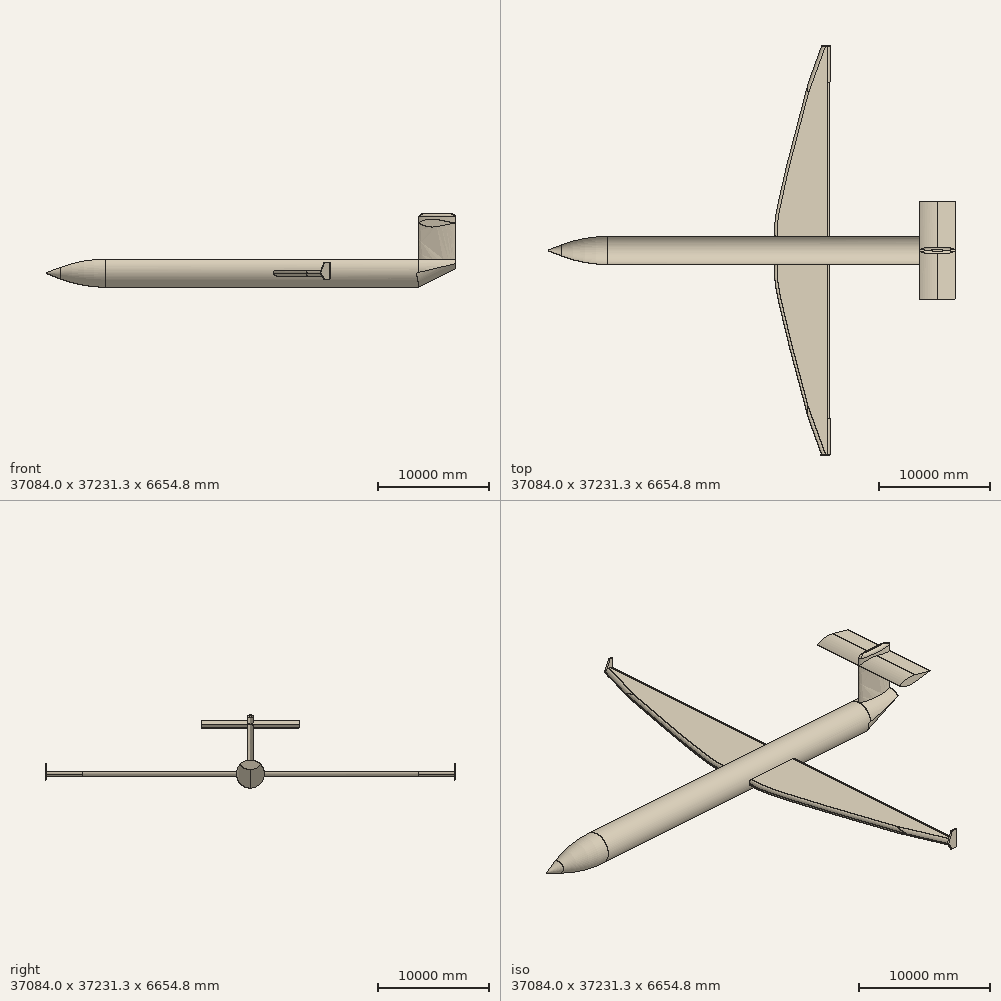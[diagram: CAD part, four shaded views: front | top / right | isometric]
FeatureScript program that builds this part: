
annotation { "Feature Type Name" : "Feature", "Feature Type Description" : "" }
export const myFeature = defineFeature(function(context is Context, id is Id, definition is map)
    precondition{}
    {
        {
            var Q0;
            Q0=qCreatedBy(makeId("Right.planeOp"),FACE);
            var sketch = newSketch(context, id + "F0", { "sketchPlane" : qUnion([Q0])});
            skCircle(sketch, "E0", {"center": v(0, 0) * mm, "radius": 1270 * mm});
            skSolve(sketch);
        }
        {
            var Q0;
            Q0=makeQuery(id+"F0.imprint","IMPRINT",FACE,{"disambiguationData":[TD([[makeQuery(id+"F0.imprint","IMPRINT",EDGE,{"derivedFrom":sQuery(id+"F0.wireOp",EDGE,"E0")}),1.0]])]});
            extrude(context, id + "F1", {"entities" : qUnion([Q0]), "endBound" : BoundingType.SYMMETRIC, "oppositeDirection" : true, "depth" : 30480 * mm, "offsetDistance" : 25.4 * mm});
        }
        {
            var Q0;
            Q0=qCreatedBy(makeId("Front.planeOp"),FACE);
            var sketch = newSketch(context, id + "F2", { "sketchPlane" : qUnion([Q0])});
            skLineSegment(sketch, "E1", {"start": v(0, 0) * mm, "end": v(0, 1270) * mm});
            skLineSegment(sketch, "E2", {"start": v(0, 1270) * mm, "end": v(15240, 1270) * mm});
            skLineSegment(sketch, "E3", {"start": v(15240, 1270) * mm, "end": v(15240, -1270) * mm});
            skLineSegment(sketch, "E4", {"start": v(15240, 1270) * mm, "end": v(18542, 1270) * mm});
            skLineSegment(sketch, "E5", {"start": v(15240, -1270) * mm, "end": v(18542, 400.65) * mm});
            skLineSegment(sketch, "E6", {"start": v(18542, 400.65) * mm, "end": v(18542, 1270) * mm});
            skSolve(sketch);
        }
        {
            var Q0;
            Q0 = qSketchRegion(id + "F2", true);
            extrude(context, id + "F3", {"entities" : qUnion([Q0]), "operationType" : NewBodyOperationType.ADD, "endBound" : BoundingType.SYMMETRIC, "depth" : 2540 * mm, "offsetDistance" : 25.4 * mm});
        }
        {
            var Q0;
            Q0=makeQuery(id+"F3.opExtrude","CAP_EDGE",EDGE,{"disambiguationData":[OSD([sQuery(id+"F2.wireOp",EDGE,"E4")])],"isStart":false});
            var Q1;
            Q1=makeQuery(id+"F3.opExtrude","CAP_EDGE",EDGE,{"disambiguationData":[OSD([sQuery(id+"F2.wireOp",EDGE,"E4")])],"isStart":true});
            var Q2;
            Q2=makeQuery(id+"F3.opExtrude","CAP_EDGE",EDGE,{"disambiguationData":[OSD([sQuery(id+"F2.wireOp",EDGE,"E5")])],"isStart":false});
            var Q3;
            Q3=makeQuery(id+"F3.opExtrude","CAP_EDGE",EDGE,{"disambiguationData":[OSD([sQuery(id+"F2.wireOp",EDGE,"E5")])],"isStart":true});
            fillet(context, id + "F4", {"entities" : qUnion([Q0, Q1, Q2, Q3]), "radius" : 1244.6 * mm, "tangentPropagation" : true, "allowEdgeOverflow" : false});
        }
        {
            var Q0;
            Q0=makeQuery(id+"F3.opExtrude","SWEPT_FACE",FACE,{"disambiguationData":[OSD([sQuery(id+"F2.wireOp",EDGE,"E4")])]});
            var sketch = newSketch(context, id + "F5", { "sketchPlane" : qUnion([Q0])});
            skEllipse(sketch, "E7", {"center": v(16891, 0) * mm, "majorRadius": 1651 * mm, "minorRadius": 317.5 * mm, "majorAxis": v(-1, 0)});
            skPoint(sketch, "E7.centerSnap0", {"position": v(16891, 25.4) * mm});
            skSolve(sketch);
        }
        {
            var Q0;
            Q0=qCreatedBy(makeId("Top.planeOp"),FACE);
            var sketch = newSketch(context, id + "F6", { "sketchPlane" : qUnion([Q0])});
            skLineSegment(sketch, "E8", {"start": v(5164.79, 15221.95) * mm, "end": v(7114.72, 15221.95) * mm});
            skLineSegment(sketch, "E9", {"start": v(7114.72, -15229.4) * mm, "end": v(5164.79, -15229.4) * mm});
            skFitSpline(sketch, "E10", {"points": [v(2139.22, 1285.92) * mm, v(2139.22, 2711.9) * mm, v(5164.79, 15221.95) * mm], "startDerivative": vector(-498.9, 4287.93) * mm, "endDerivative": vector(5531.34, 20770.7) * mm});
            skFitSpline(sketch, "E11", {"points": [v(2131.34, -1268.74) * mm, v(2131.34, -2790.45) * mm, v(5164.79, -15229.4) * mm], "startDerivative": vector(-524.47, -4573.38) * mm, "endDerivative": vector(5598.9, -20746.14) * mm});
            skLineSegment(sketch, "E12", {"start": v(7114.72, -1259.38) * mm, "end": v(7114.72, -15229.4) * mm});
            skLineSegment(sketch, "E13", {"start": v(7114.72, 1309.17) * mm, "end": v(7114.72, 15221.95) * mm});
            skLineSegment(sketch, "E14", {"start": v(7114.72, 1309.17) * mm, "end": v(7114.72, -1259.38) * mm});
            skLineSegment(sketch, "E15", {"start": v(2139.22, 1285.92) * mm, "end": v(2131.34, -1268.74) * mm});
            skSolve(sketch);
        }
        {
            var Q0;
            Q0 = qSketchRegion(id + "F6", true);
            extrude(context, id + "F7", {"entities" : qUnion([Q0]), "operationType" : NewBodyOperationType.ADD, "endBound" : BoundingType.SYMMETRIC, "depth" : 508 * mm, "offsetDistance" : 25.4 * mm});
        }
        {
            var Q0;
            {var subQ0=sQuery(id+"F6.wireOp",EDGE,"E15");var subQ1=sQuery(id+"F6.wireOp",EDGE,"E10");Q0=makeQuery(id+"F7.boolean.opBoolean","SPLIT",EDGE,{"disambiguationData":[TD([makeQuery(id+"F7.opExtrude","SWEPT_FACE",FACE,{"disambiguationData":[OSD([subQ1])]})])],"derivedFrom":makeQuery(id+"F7.opExtrude","CAP_EDGE",EDGE,{"disambiguationData":[OSD([subQ0])],"isStart":true})});}
            var Q1;
            Q1=makeQuery(id+"F7.opExtrude","CAP_EDGE",EDGE,{"disambiguationData":[OSD([sQuery(id+"F6.wireOp",EDGE,"E10")])],"isStart":true});
            var Q2;
            {var subQ0=sQuery(id+"F6.wireOp",EDGE,"E15");var subQ1=sQuery(id+"F6.wireOp",EDGE,"E10");Q2=makeQuery(id+"F7.boolean.opBoolean","SPLIT",EDGE,{"disambiguationData":[TD([makeQuery(id+"F7.opExtrude","SWEPT_FACE",FACE,{"disambiguationData":[OSD([subQ1])]})])],"derivedFrom":makeQuery(id+"F7.opExtrude","CAP_EDGE",EDGE,{"disambiguationData":[OSD([subQ0])],"isStart":false})});}
            var Q3;
            Q3=makeQuery(id+"F7.opExtrude","CAP_EDGE",EDGE,{"disambiguationData":[OSD([sQuery(id+"F6.wireOp",EDGE,"E10")])],"isStart":false});
            fillet(context, id + "F8", {"entities" : qUnion([Q0, Q1, Q2, Q3]), "radius" : 254 * mm, "tangentPropagation" : true, "allowEdgeOverflow" : false});
        }
        {
            var Q0;
            Q0=makeQuery(id+"F7.opExtrude","CAP_EDGE",EDGE,{"disambiguationData":[OSD([sQuery(id+"F6.wireOp",EDGE,"E11")])],"isStart":false});
            var Q1;
            Q1=makeQuery(id+"F7.opExtrude","CAP_EDGE",EDGE,{"disambiguationData":[OSD([sQuery(id+"F6.wireOp",EDGE,"E11")])],"isStart":true});
            var Q2;
            {var subQ0=sQuery(id+"F6.wireOp",EDGE,"E15");var subQ1=sQuery(id+"F6.wireOp",EDGE,"E11");Q2=makeQuery(id+"F7.boolean.opBoolean","SPLIT",EDGE,{"disambiguationData":[TD([makeQuery(id+"F7.opExtrude","SWEPT_FACE",FACE,{"disambiguationData":[OSD([subQ1])]})])],"derivedFrom":makeQuery(id+"F7.opExtrude","CAP_EDGE",EDGE,{"disambiguationData":[OSD([subQ0])],"isStart":true})});}
            var Q3;
            {var subQ0=sQuery(id+"F6.wireOp",EDGE,"E15");var subQ1=sQuery(id+"F6.wireOp",EDGE,"E11");Q3=makeQuery(id+"F7.boolean.opBoolean","SPLIT",EDGE,{"disambiguationData":[TD([makeQuery(id+"F7.opExtrude","SWEPT_FACE",FACE,{"disambiguationData":[OSD([subQ1])]})])],"derivedFrom":makeQuery(id+"F7.opExtrude","CAP_EDGE",EDGE,{"disambiguationData":[OSD([subQ0])],"isStart":false})});}
            fillet(context, id + "F9", {"entities" : qUnion([Q0, Q1, Q2, Q3]), "radius" : 254 * mm, "tangentPropagation" : true, "allowEdgeOverflow" : false});
        }
        {
            var Q0;
            {var subQ0=sQuery(id+"F6.wireOp",EDGE,"E9");var subQ1=sQuery(id+"F6.wireOp",EDGE,"E14");var subQ2=sQuery(id+"F6.wireOp",EDGE,"E13");var subQ3=sQuery(id+"F6.wireOp",EDGE,"E12");Q0=makeQuery(id+"F7.boolean.opBoolean","SPLIT",EDGE,{"disambiguationData":[TD([makeQuery(id+"F7.opExtrude","SWEPT_FACE",FACE,{"disambiguationData":[OSD([subQ0])]})])],"derivedFrom":makeQuery(id+"F7.opExtrude","CAP_EDGE",EDGE,{"disambiguationData":[OSD([subQ3,subQ2,subQ1])],"isStart":false})});}
            var Q1;
            {var subQ0=sQuery(id+"F6.wireOp",EDGE,"E9");var subQ1=sQuery(id+"F6.wireOp",EDGE,"E14");var subQ2=sQuery(id+"F6.wireOp",EDGE,"E13");var subQ3=sQuery(id+"F6.wireOp",EDGE,"E12");Q1=makeQuery(id+"F7.boolean.opBoolean","SPLIT",EDGE,{"disambiguationData":[TD([makeQuery(id+"F7.opExtrude","SWEPT_FACE",FACE,{"disambiguationData":[OSD([subQ0])]})])],"derivedFrom":makeQuery(id+"F7.opExtrude","CAP_EDGE",EDGE,{"disambiguationData":[OSD([subQ3,subQ2,subQ1])],"isStart":true})});}
            var Q2;
            {var subQ0=sQuery(id+"F6.wireOp",EDGE,"E8");var subQ1=sQuery(id+"F6.wireOp",EDGE,"E14");var subQ2=sQuery(id+"F6.wireOp",EDGE,"E13");var subQ3=sQuery(id+"F6.wireOp",EDGE,"E12");Q2=makeQuery(id+"F7.boolean.opBoolean","SPLIT",EDGE,{"disambiguationData":[TD([makeQuery(id+"F7.opExtrude","SWEPT_FACE",FACE,{"disambiguationData":[OSD([subQ0])]})])],"derivedFrom":makeQuery(id+"F7.opExtrude","CAP_EDGE",EDGE,{"disambiguationData":[OSD([subQ3,subQ2,subQ1])],"isStart":false})});}
            var Q3;
            {var subQ0=sQuery(id+"F6.wireOp",EDGE,"E8");var subQ1=sQuery(id+"F6.wireOp",EDGE,"E14");var subQ2=sQuery(id+"F6.wireOp",EDGE,"E13");var subQ3=sQuery(id+"F6.wireOp",EDGE,"E12");Q3=makeQuery(id+"F7.boolean.opBoolean","SPLIT",EDGE,{"disambiguationData":[TD([makeQuery(id+"F7.opExtrude","SWEPT_FACE",FACE,{"disambiguationData":[OSD([subQ0])]})])],"derivedFrom":makeQuery(id+"F7.opExtrude","CAP_EDGE",EDGE,{"disambiguationData":[OSD([subQ3,subQ2,subQ1])],"isStart":true})});}
            fillet(context, id + "F10", {"entities" : qUnion([Q0, Q1, Q2, Q3]), "radius" : 254 * mm, "tangentPropagation" : true, "allowEdgeOverflow" : false});
        }
        {
            var Q0;
            Q0=qCreatedBy(makeId("Top.planeOp"),FACE);
            var sketch = newSketch(context, id + "F11", { "sketchPlane" : qUnion([Q0])});
            skLineSegment(sketch, "E16", {"start": v(0, 0) * mm, "end": v(6350, 0) * mm});
            skLineSegment(sketch, "E17", {"start": v(6334.3, -18488.63) * mm, "end": v(5142.28, -15211.2) * mm});
            skLineSegment(sketch, "E18", {"start": v(5142.28, -15211.2) * mm, "end": v(7148.88, -15211.2) * mm});
            skLineSegment(sketch, "E19", {"start": v(7148.88, -15211.2) * mm, "end": v(7148.88, -18488.63) * mm});
            skLineSegment(sketch, "E20", {"start": v(7148.88, -18488.63) * mm, "end": v(6334.3, -18488.63) * mm});
            skLineSegment(sketch, "E21.MirrorCS", {"start": v(7148.88, 18488.63) * mm, "end": v(6334.3, 18488.63) * mm});
            skLineSegment(sketch, "E22.MirrorCS", {"start": v(5142.28, 15211.2) * mm, "end": v(7148.88, 15211.2) * mm});
            skLineSegment(sketch, "E23.MirrorCS", {"start": v(6334.3, 18488.63) * mm, "end": v(5142.28, 15211.2) * mm});
            skLineSegment(sketch, "E24.MirrorCS", {"start": v(7148.88, 15211.2) * mm, "end": v(7148.88, 18488.63) * mm});
            skSolve(sketch);
        }
        {
            var Q0;
            Q0 = qSketchRegion(id + "F11", true);
            extrude(context, id + "F12", {"entities" : qUnion([Q0]), "operationType" : NewBodyOperationType.ADD, "endBound" : BoundingType.SYMMETRIC, "depth" : 508 * mm, "offsetDistance" : 25.4 * mm});
        }
        {
            var Q0;
            Q0=makeQuery(id+"F12.opExtrude","CAP_EDGE",EDGE,{"disambiguationData":[OSD([sQuery(id+"F11.wireOp",EDGE,"E17")])],"isStart":false});
            var Q1;
            Q1=makeQuery(id+"F12.opExtrude","CAP_EDGE",EDGE,{"disambiguationData":[OSD([sQuery(id+"F11.wireOp",EDGE,"E17")])],"isStart":true});
            fillet(context, id + "F13", {"entities" : qUnion([Q0, Q1]), "radius" : 355.6 * mm, "tangentPropagation" : true, "allowEdgeOverflow" : false});
        }
        {
            var Q0;
            Q0=makeQuery(id+"F12.opExtrude","CAP_EDGE",EDGE,{"disambiguationData":[OSD([sQuery(id+"F11.wireOp",EDGE,"E19")])],"isStart":true});
            var Q1;
            Q1=makeQuery(id+"F12.opExtrude","CAP_EDGE",EDGE,{"disambiguationData":[OSD([sQuery(id+"F11.wireOp",EDGE,"E19")])],"isStart":false});
            fillet(context, id + "F14", {"entities" : qUnion([Q0, Q1]), "radius" : 279.4 * mm, "tangentPropagation" : true, "allowEdgeOverflow" : false});
        }
        {
            var Q0;
            {var subQ1=sQuery(id+"F11.wireOp",EDGE,"E19");var subQ2=sQuery(id+"F11.wireOp",EDGE,"E18");Q0=makeQuery(id+"F14.opFillet","BLEND_EDGE",EDGE,{"blendedFrom":[makeQuery(id+"F12.opExtrude","CAP_EDGE",EDGE,{"disambiguationData":[OSD([subQ1])],"isStart":false}),makeQuery(id+"F12.boolean.opBoolean","SPLIT",FACE,{"disambiguationData":[TD([makeQuery(id+"F12.opExtrude","SWEPT_FACE",FACE,{"disambiguationData":[OSD([subQ1])]})])],"derivedFrom":makeQuery(id+"F12.opExtrude","SWEPT_FACE",FACE,{"disambiguationData":[OSD([subQ2])]})})],"blendedInto":[makeQuery(id+"F12.boolean.opBoolean","SPLIT",FACE,{"disambiguationData":[TD([makeQuery(id+"F12.opExtrude","SWEPT_FACE",FACE,{"disambiguationData":[OSD([subQ1])]})])],"derivedFrom":makeQuery(id+"F12.opExtrude","SWEPT_FACE",FACE,{"disambiguationData":[OSD([subQ2])]})})]});}
            var Q1;
            {var subQ1=sQuery(id+"F11.wireOp",EDGE,"E19");var subQ2=sQuery(id+"F11.wireOp",EDGE,"E18");Q1=makeQuery(id+"F14.opFillet","BLEND_EDGE",EDGE,{"blendedFrom":[makeQuery(id+"F12.opExtrude","CAP_EDGE",EDGE,{"disambiguationData":[OSD([subQ1])],"isStart":true}),makeQuery(id+"F12.boolean.opBoolean","SPLIT",FACE,{"disambiguationData":[TD([makeQuery(id+"F12.opExtrude","SWEPT_FACE",FACE,{"disambiguationData":[OSD([subQ1])]})])],"derivedFrom":makeQuery(id+"F12.opExtrude","SWEPT_FACE",FACE,{"disambiguationData":[OSD([subQ2])]})})],"blendedInto":[makeQuery(id+"F12.boolean.opBoolean","SPLIT",FACE,{"disambiguationData":[TD([makeQuery(id+"F12.opExtrude","SWEPT_FACE",FACE,{"disambiguationData":[OSD([subQ1])]})])],"derivedFrom":makeQuery(id+"F12.opExtrude","SWEPT_FACE",FACE,{"disambiguationData":[OSD([subQ2])]})})]});}
            fillet(context, id + "F15", {"entities" : qUnion([Q0, Q1]), "radius" : 101.6 * mm, "tangentPropagation" : true, "allowEdgeOverflow" : false});
        }
        {
            var Q0;
            Q0=makeQuery(id+"F12.opExtrude","CAP_EDGE",EDGE,{"disambiguationData":[OSD([sQuery(id+"F11.wireOp",EDGE,"E23.MirrorCS")])],"isStart":false});
            var Q1;
            Q1=makeQuery(id+"F12.opExtrude","CAP_EDGE",EDGE,{"disambiguationData":[OSD([sQuery(id+"F11.wireOp",EDGE,"E23.MirrorCS")])],"isStart":true});
            fillet(context, id + "F16", {"entities" : qUnion([Q0, Q1]), "radius" : 355.6 * mm, "tangentPropagation" : true, "allowEdgeOverflow" : false});
        }
        {
            var Q0;
            Q0=makeQuery(id+"F12.opExtrude","CAP_EDGE",EDGE,{"disambiguationData":[OSD([sQuery(id+"F11.wireOp",EDGE,"E24.MirrorCS")])],"isStart":false});
            var Q1;
            Q1=makeQuery(id+"F12.opExtrude","CAP_EDGE",EDGE,{"disambiguationData":[OSD([sQuery(id+"F11.wireOp",EDGE,"E24.MirrorCS")])],"isStart":true});
            fillet(context, id + "F17", {"entities" : qUnion([Q0, Q1]), "radius" : 279.4 * mm, "tangentPropagation" : true, "allowEdgeOverflow" : false});
        }
        {
            var Q0;
            {var subQ0=sQuery(id+"F11.wireOp",EDGE,"E24.MirrorCS");var subQ2=sQuery(id+"F11.wireOp",EDGE,"E22.MirrorCS");Q0=makeQuery(id+"F17.opFillet","BLEND_EDGE",EDGE,{"blendedFrom":[makeQuery(id+"F12.opExtrude","CAP_EDGE",EDGE,{"disambiguationData":[OSD([subQ0])],"isStart":false}),makeQuery(id+"F12.boolean.opBoolean","SPLIT",FACE,{"disambiguationData":[TD([makeQuery(id+"F12.opExtrude","SWEPT_FACE",FACE,{"disambiguationData":[OSD([subQ0])]})])],"derivedFrom":makeQuery(id+"F12.opExtrude","SWEPT_FACE",FACE,{"disambiguationData":[OSD([subQ2])]})})],"blendedInto":[makeQuery(id+"F12.boolean.opBoolean","SPLIT",FACE,{"disambiguationData":[TD([makeQuery(id+"F12.opExtrude","SWEPT_FACE",FACE,{"disambiguationData":[OSD([subQ0])]})])],"derivedFrom":makeQuery(id+"F12.opExtrude","SWEPT_FACE",FACE,{"disambiguationData":[OSD([subQ2])]})})]});}
            var Q1;
            {var subQ0=sQuery(id+"F11.wireOp",EDGE,"E24.MirrorCS");var subQ2=sQuery(id+"F11.wireOp",EDGE,"E22.MirrorCS");Q1=makeQuery(id+"F17.opFillet","BLEND_EDGE",EDGE,{"blendedFrom":[makeQuery(id+"F12.opExtrude","CAP_EDGE",EDGE,{"disambiguationData":[OSD([subQ0])],"isStart":true}),makeQuery(id+"F12.boolean.opBoolean","SPLIT",FACE,{"disambiguationData":[TD([makeQuery(id+"F12.opExtrude","SWEPT_FACE",FACE,{"disambiguationData":[OSD([subQ0])]})])],"derivedFrom":makeQuery(id+"F12.opExtrude","SWEPT_FACE",FACE,{"disambiguationData":[OSD([subQ2])]})})],"blendedInto":[makeQuery(id+"F12.boolean.opBoolean","SPLIT",FACE,{"disambiguationData":[TD([makeQuery(id+"F12.opExtrude","SWEPT_FACE",FACE,{"disambiguationData":[OSD([subQ0])]})])],"derivedFrom":makeQuery(id+"F12.opExtrude","SWEPT_FACE",FACE,{"disambiguationData":[OSD([subQ2])]})})]});}
            fillet(context, id + "F18", {"entities" : qUnion([Q0, Q1]), "radius" : 101.6 * mm, "tangentPropagation" : true, "allowEdgeOverflow" : false});
        }
        {
            var Q0;
            Q0=makeQuery(id+"F12.opExtrude","SWEPT_FACE",FACE,{"disambiguationData":[OSD([sQuery(id+"F11.wireOp",EDGE,"E21.MirrorCS")])]});
            var sketch = newSketch(context, id + "F19", { "sketchPlane" : qUnion([Q0])});
            skLineSegment(sketch, "E25", {"start": v(-7147.72, 0) * mm, "end": v(-7147.72, 984.63) * mm});
            skLineSegment(sketch, "E26", {"start": v(-7147.72, -589.48) * mm, "end": v(-7147.72, 0) * mm});
            skLineSegment(sketch, "E27", {"start": v(-7147.72, 984.63) * mm, "end": v(-6766.72, 984.63) * mm});
            skLineSegment(sketch, "E28", {"start": v(-6766.72, 984.63) * mm, "end": v(-6313.3, 0) * mm});
            skLineSegment(sketch, "E29", {"start": v(-7147.72, -589.48) * mm, "end": v(-6766.72, -589.48) * mm});
            skLineSegment(sketch, "E30", {"start": v(-6766.72, -589.48) * mm, "end": v(-6313.3, 0) * mm});
            skSolve(sketch);
        }
        {
            var Q0;
            Q0 = qSketchRegion(id + "F19", true);
            extrude(context, id + "F20", {"entities" : qUnion([Q0]), "operationType" : NewBodyOperationType.ADD, "depth" : 127 * mm, "offsetDistance" : 25.4 * mm});
        }
        {
            var Q0;
            Q0=makeQuery(id+"F20.opExtrude","CAP_EDGE",EDGE,{"disambiguationData":[OSD([sQuery(id+"F19.wireOp",EDGE,"E30")])],"isStart":true});
            var Q1;
            Q1=makeQuery(id+"F20.opExtrude","CAP_EDGE",EDGE,{"disambiguationData":[OSD([sQuery(id+"F19.wireOp",EDGE,"E30")])],"isStart":false});
            var Q2;
            Q2=makeQuery(id+"F20.opExtrude","CAP_EDGE",EDGE,{"disambiguationData":[OSD([sQuery(id+"F19.wireOp",EDGE,"E28")])],"isStart":false});
            var Q3;
            Q3=makeQuery(id+"F20.opExtrude","CAP_EDGE",EDGE,{"disambiguationData":[OSD([sQuery(id+"F19.wireOp",EDGE,"E28")])],"isStart":true});
            fillet(context, id + "F21", {"entities" : qUnion([Q0, Q1, Q2, Q3]), "radius" : 63.5 * mm, "tangentPropagation" : true, "allowEdgeOverflow" : false});
        }
        {
            var Q0;
            {var subQ0=sQuery(id+"F19.wireOp",EDGE,"E26");var subQ1=sQuery(id+"F19.wireOp",EDGE,"E25");var subQ3=sQuery(id+"F19.wireOp",EDGE,"E29");Q0=makeQuery(id+"F20.boolean.opBoolean","SPLIT",EDGE,{"disambiguationData":[TD([makeQuery(id+"F20.opExtrude","SWEPT_FACE",FACE,{"disambiguationData":[OSD([subQ3])]})])],"derivedFrom":makeQuery(id+"F20.opExtrude","CAP_EDGE",EDGE,{"disambiguationData":[OSD([subQ1,subQ0])],"isStart":true})});}
            var Q1;
            {var subQ0=sQuery(id+"F19.wireOp",EDGE,"E26");var subQ1=sQuery(id+"F19.wireOp",EDGE,"E25");var subQ3=sQuery(id+"F19.wireOp",EDGE,"E27");Q1=makeQuery(id+"F20.boolean.opBoolean","SPLIT",EDGE,{"disambiguationData":[TD([makeQuery(id+"F20.opExtrude","SWEPT_FACE",FACE,{"disambiguationData":[OSD([subQ3])]})])],"derivedFrom":makeQuery(id+"F20.opExtrude","CAP_EDGE",EDGE,{"disambiguationData":[OSD([subQ1,subQ0])],"isStart":true})});}
            var Q2;
            Q2=makeQuery(id+"F20.opExtrude","CAP_EDGE",EDGE,{"disambiguationData":[OSD([sQuery(id+"F19.wireOp",EDGE,"E25"),sQuery(id+"F19.wireOp",EDGE,"E26")])],"isStart":false});
            fillet(context, id + "F22", {"entities" : qUnion([Q0, Q1, Q2]), "radius" : 63.5 * mm, "tangentPropagation" : true, "allowEdgeOverflow" : false});
        }
        {
            var Q0;
            Q0=makeQuery(id+"F12.opExtrude","SWEPT_FACE",FACE,{"disambiguationData":[OSD([sQuery(id+"F11.wireOp",EDGE,"E20")])]});
            var sketch = newSketch(context, id + "F23", { "sketchPlane" : qUnion([Q0])});
            skPoint(sketch, "E31.startSnap0", {"position": v(7091.08, 101.6) * mm});
            skLineSegment(sketch, "E32", {"start": v(7218.08, 980.48) * mm, "end": v(7218.08, -588.34) * mm});
            skLineSegment(sketch, "E33", {"start": v(7218.08, 980.48) * mm, "end": v(6659.28, 980.48) * mm});
            skLineSegment(sketch, "E34", {"start": v(7218.08, -588.34) * mm, "end": v(6659.28, -588.34) * mm});
            skLineSegment(sketch, "E35", {"start": v(6659.28, -588.34) * mm, "end": v(6286.26, 0) * mm});
            skLineSegment(sketch, "E36", {"start": v(6286.26, 0) * mm, "end": v(6659.28, 980.48) * mm});
            skSolve(sketch);
        }
        {
            var Q0;
            Q0 = qSketchRegion(id + "F23", true);
            extrude(context, id + "F24", {"entities" : qUnion([Q0]), "operationType" : NewBodyOperationType.ADD, "depth" : 127 * mm, "offsetDistance" : 25.4 * mm});
        }
        {
            var Q0;
            Q0=makeQuery(id+"F24.opExtrude","CAP_EDGE",EDGE,{"disambiguationData":[OSD([sQuery(id+"F23.wireOp",EDGE,"E36")])],"isStart":false});
            var Q1;
            Q1=makeQuery(id+"F24.opExtrude","CAP_EDGE",EDGE,{"disambiguationData":[OSD([sQuery(id+"F23.wireOp",EDGE,"E36")])],"isStart":true});
            var Q2;
            Q2=makeQuery(id+"F24.opExtrude","CAP_EDGE",EDGE,{"disambiguationData":[OSD([sQuery(id+"F23.wireOp",EDGE,"E35")])],"isStart":true});
            var Q3;
            Q3=makeQuery(id+"F24.opExtrude","CAP_EDGE",EDGE,{"disambiguationData":[OSD([sQuery(id+"F23.wireOp",EDGE,"E35")])],"isStart":false});
            fillet(context, id + "F25", {"entities" : qUnion([Q0, Q1, Q2, Q3]), "radius" : 63.5 * mm, "tangentPropagation" : true, "allowEdgeOverflow" : false});
        }
        {
            var Q0;
            Q0=makeQuery(id+"F24.opExtrude","CAP_EDGE",EDGE,{"disambiguationData":[OSD([sQuery(id+"F23.wireOp",EDGE,"E32")])],"isStart":false});
            var Q1;
            Q1=makeQuery(id+"F24.opExtrude","CAP_EDGE",EDGE,{"disambiguationData":[OSD([sQuery(id+"F23.wireOp",EDGE,"E32")])],"isStart":true});
            fillet(context, id + "F26", {"entities" : qUnion([Q0, Q1]), "radius" : 63.5 * mm, "tangentPropagation" : true, "allowEdgeOverflow" : false});
        }
        {
            var Q0;
            Q0 = qSketchRegion(id + "F5", true);
            extrude(context, id + "F27", {"entities" : qUnion([Q0]), "operationType" : NewBodyOperationType.ADD, "depth" : 50.8 * mm, "offsetDistance" : 25.4 * mm});
        }
        {
            var Q0;
            Q0=makeQuery(id+"F27.opExtrude","CAP_FACE",FACE,{"disambiguationData":[OSD([sQuery(id+"F5.wireOp",EDGE,"E7")])],"isStart":false});
            var sketch = newSketch(context, id + "F28", { "sketchPlane" : qUnion([Q0])});
            skEllipse(sketch, "E37", {"center": v(16891, 0) * mm, "majorRadius": 1651 * mm, "minorRadius": 317.5 * mm, "majorAxis": v(-1, 0)});
            skSolve(sketch);
        }
        {
            var Q0;
            Q0=makeQuery(id+"F28.imprint","IMPRINT",FACE,{"disambiguationData":[TD([[makeQuery(id+"F28.imprint","IMPRINT",EDGE,{"derivedFrom":sQuery(id+"F28.wireOp",EDGE,"E37")}),1.0]])]});
            extrude(context, id + "F29", {"entities" : qUnion([Q0]), "operationType" : NewBodyOperationType.ADD, "depth" : 4064 * mm, "offsetDistance" : 25.4 * mm});
        }
        {
            var Q0;
            Q0=qCreatedBy(makeId("Front.planeOp"),FACE);
            var sketch = newSketch(context, id + "F30", { "sketchPlane" : qUnion([Q0])});
            skLineSegment(sketch, "E38", {"start": v(16891, 4855.27) * mm, "end": v(18542, 4537.77) * mm});
            skLineSegment(sketch, "E39", {"start": v(18542, 4537.77) * mm, "end": v(16891, 4220.27) * mm});
            skArc(sketch, "E40", {"start": v(15233.8, 4537.77) * mm, "mid": v(16031.92, 4219.97) * mm, "end": v(16891, 4220.27) * mm});
            skArc(sketch, "E41", {"start": v(16891, 4855.27) * mm, "mid": v(16031.92, 4855.57) * mm, "end": v(15233.8, 4537.77) * mm});
            skSolve(sketch);
        }
        {
            var Q0;
            Q0 = qSketchRegion(id + "F30", true);
            extrude(context, id + "F31", {"entities" : qUnion([Q0]), "operationType" : NewBodyOperationType.ADD, "endBound" : BoundingType.SYMMETRIC, "depth" : 8890 * mm, "offsetDistance" : 25.4 * mm});
        }
        {
            var Q0;
            Q0=makeQuery(id+"F29.opExtrude","CAP_EDGE",EDGE,{"disambiguationData":[OSD([sQuery(id+"F28.wireOp",EDGE,"E37")])],"isStart":false});
            fillet(context, id + "F32", {"entities" : qUnion([Q0]), "radius" : 254 * mm, "tangentPropagation" : true, "allowEdgeOverflow" : false});
        }
        {
            var Q0;
            Q0=qCreatedBy(makeId("Front.planeOp"),FACE);
            var sketch = newSketch(context, id + "F33", { "sketchPlane" : qUnion([Q0])});
            skLineSegment(sketch, "E42", {"start": v(-15240, 0) * mm, "end": v(-18542, 0) * mm});
            skLineSegment(sketch, "E43", {"start": v(-15240, 0) * mm, "end": v(-15240, 1270) * mm});
            skLineSegment(sketch, "E44", {"start": v(-15240, 1270) * mm, "end": v(-18542, 0) * mm});
            skLineSegment(sketch, "E45", {"start": v(0, 0) * mm, "end": v(-21713.36, 0) * mm});
            skSolve(sketch);
        }
        {
            var Q0;
            {var subQ0=sQuery(id+"F33.wireOp",EDGE,"E43");Q0=makeQuery(id+"F33.imprint","IMPRINT",FACE,{"disambiguationData":[TD([[makeQuery(id+"F33.imprint","IMPRINT",EDGE,{"derivedFrom":subQ0}),1.0]])]});}
            var Q1;
            Q1=sQuery(id+"F33.wireOp",EDGE,"E45");
            revolve(context, id + "F34", {"operationType" : NewBodyOperationType.ADD, "surfaceOperationType" : NewSurfaceOperationType.NEW, "entities" : qUnion([Q0]), "axis" : qUnion([Q1]), "revolveType" : RevolveType.FULL});
        }
        {
            var Q0;
            Q0=makeQuery(id+"F34.opRevolve","SWEPT_FACE",FACE,{"disambiguationData":[OSD([sQuery(id+"F33.wireOp",EDGE,"E44")])]});
            fillet(context, id + "F35", {"entities" : qUnion([Q0]), "radius" : 11430 * mm, "tangentPropagation" : true, "allowEdgeOverflow" : false});
        }
        {
            var Q0;
            Q0 = qSketchRegion(id + "F5", true);
            extrude(context, id + "F36", {"entities" : qUnion([Q0]), "operationType" : NewBodyOperationType.ADD, "oppositeDirection" : true, "depth" : 76.2 * mm, "offsetDistance" : 25.4 * mm});
        }
    });
